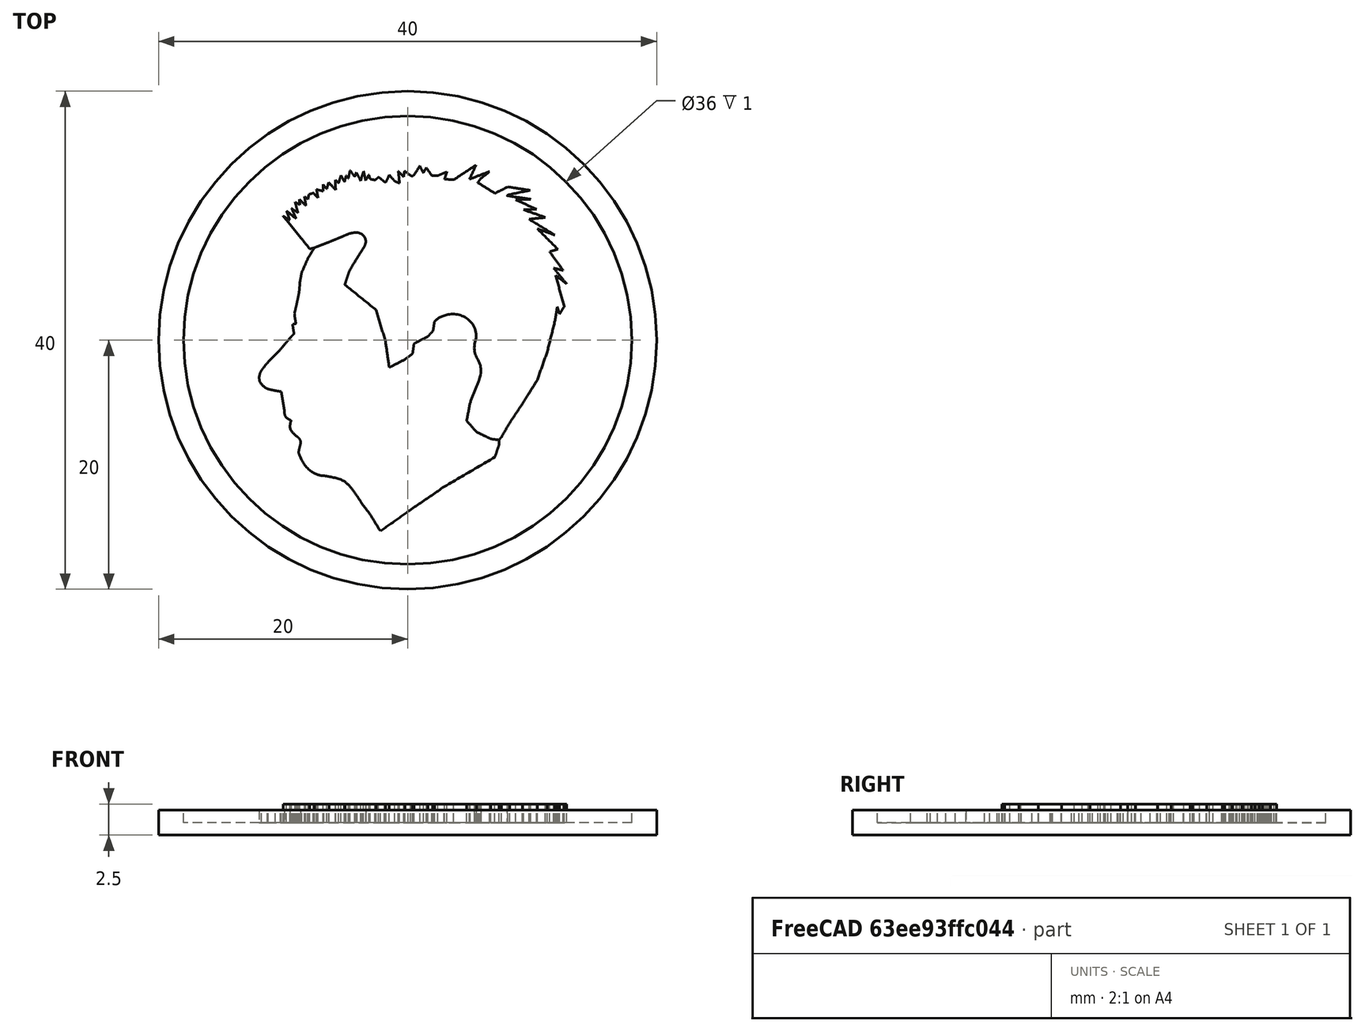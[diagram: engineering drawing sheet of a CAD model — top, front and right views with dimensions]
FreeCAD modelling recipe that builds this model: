
FCSTD DOCUMENT  (FreeCAD 0.17R13217 (Git))
Label: perfil-obijuan3
License: All rights reserved
LicenseURL: http://en.wikipedia.org/wiki/All_rights_reserved
objects: Part::Feature×2, Part::Extrusion×2, Part::Cylinder×2, Part::Cut×1, Part::MultiFuse×1
note: 8 computed .brp shape members not serialized (recipe doc carries the construction recipe); baked Part::Feature solids carry a one-line shape summary decoded from their .brp

FEATURE [Part::Feature] Wire
  shape: bbox 19.31 x 24.07 x 2e-07 mm, 0 faces, 0 solids (baked)
FEATURE [Part::Extrusion] Extrude
  Base = -> Wire
  Dir = (0,0,-1)
  DirMode = 2
  FaceMakerClass = Part::FaceMakerBullseye
  LengthFwd = 1
  LengthRev = 0
  Placement = pos=(-19.6201,19.8391,1) rot=(0,0,1;0rad)
  Reversed = true
  Solid = true
  Symmetric = false
FEATURE [Part::Feature] Wire001
  shape: bbox 22.78 x 22.08 x 2e-07 mm, 0 faces, 0 solids (baked)
FEATURE [Part::Extrusion] Extrude001
  Base = -> Wire001
  Dir = (0,0,1)
  DirMode = 2
  FaceMakerClass = Part::FaceMakerBullseye
  LengthFwd = 1.5
  LengthRev = 0
  Placement = pos=(-19.6201,19.8391,1) rot=(0,0,1;0rad)
  Solid = true
  Symmetric = false
FEATURE [Part::Cylinder] Cylinder  label="Cilindro"
  Angle = 360
  AttacherType = Attacher::AttachEngine3D
  Height = 2
  Radius = 20
FEATURE [Part::Cylinder] Cylinder001  label="Cilindro001"
  Angle = 360
  AttacherType = Attacher::AttachEngine3D
  Height = 2
  Placement = pos=(0,0,1) rot=(0,0,1;0rad)
  Radius = 18
FEATURE [Part::Cut] Cut
  Base = -> Cylinder
  Refine = true
  Tool = -> Cylinder001
FEATURE [Part::MultiFuse] Fusion
  Refine = true
  Shapes = -> [Cut,Extrude]
